# Revit family: HL_RU_Roof drain_HL64FSafe-B-221103
name_source: partatom
category: Sanitärinstallationen
units: mm (PartAtom-declared; Revit-internal decimal feet)

## family parameters
Arbeitsebenenbasiert = Nein
Beim Laden mit Abzugskörper schneiden = Nein
Bemaßung runder Anschluss = Durchmesser verwenden
Gemeinsam genutzt = Nein
Immer vertikal = Ja
OmniClass-Nummer = 23.70.50.21.24.14
OmniClass-Titel = Deck Waste Water Drains
Raumberechnungspunkt = Ja
Teiletyp = Normal

## types (2) — shared parameters
Abwasserrohrverbindung = Ja
Beschreibung = Кровельные воронки
HW-Verbindung = Nein
Hersteller = HL Hutterer & Lechner GmbH
KW-Verbindung = Nein
Lüftungsverbindung = Nein
URL = http://www.hutterer-lechner.com
ВЫСОТА МОНТАЖА = 150mm
МАТЕРИАЛ = PP
РЕШЁТКА = Laubfangkorb d 262 mm
zero-valued in all types: Vorgabe-Ansicht

## per-type parameters (varying)
| type | Bauelement | EAN | Modell | Typenkommentare | ВЕС | НОМИНАЛЬНЫЙ ДИАМЕТР | РАЗМЕР |
| HL_Кровельная воронка_HL64FSafe_1 | HL64FSafe_1 | 9003076041008 | HL64FSafe_1 | HL64FSafe/1, Воронка для аварийного водостока с горизонтальным выпуском DN110 с корпусом из ПП, с возможностью регулировки толщины слоя воды | 2,273 [kg] | 110 mm | DN110 |
| HL_Кровельная воронка_HL64FSafe_7 | HL64FSafe_7 | 9003076040995 | HL64FSafe_7 | HL64FSafe/7, Воронка для аварийного водостока с горизонтальным выпуском DN75 с корпусом из ПП, с возможностью регулировки толщины слоя воды | 2,163 [kg] | 75 mm | DN75 |

## geometry (parser evidence)
native form markers: Sweep x2
no freeform markers — native parametric forms only
